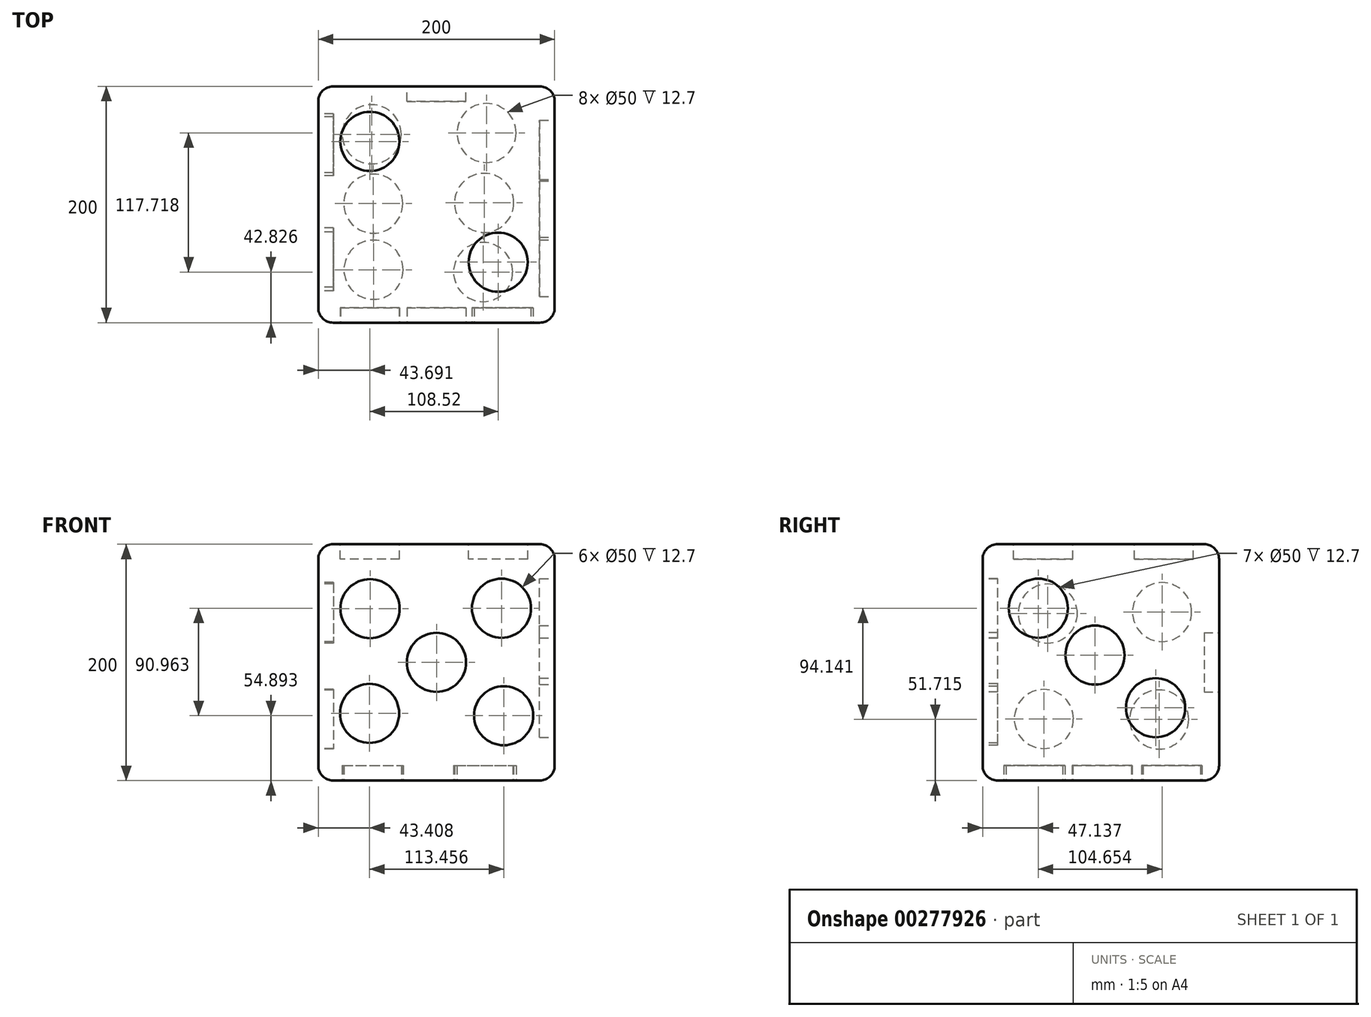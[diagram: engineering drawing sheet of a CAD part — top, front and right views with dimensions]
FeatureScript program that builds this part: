
annotation { "Feature Type Name" : "Feature", "Feature Type Description" : "" }
export const myFeature = defineFeature(function(context is Context, id is Id, definition is map)
    precondition{}
    {
        {
            var Q0;
            Q0=qCreatedBy(makeId("Front.planeOp"),FACE);
            var sketch = newSketch(context, id + "F0", { "sketchPlane" : qUnion([Q0])});
            skLineSegment(sketch, "E0.bottom", {"start": v(100, -100) * mm, "end": v(-100, -100) * mm});
            skLineSegment(sketch, "E0.top", {"start": v(100, 100) * mm, "end": v(-100, 100) * mm});
            skLineSegment(sketch, "E0.left", {"start": v(100, -100) * mm, "end": v(100, 100) * mm});
            skLineSegment(sketch, "E0.right", {"start": v(-100, -100) * mm, "end": v(-100, 100) * mm});
            skPoint(sketch, "E0.middle", {"position": v(0, 0) * mm});
            skSolve(sketch);
        }
        {
            var Q0;
            Q0 = qSketchRegion(id + "F0", true);
            extrude(context, id + "F1", {"entities" : qUnion([Q0]), "depth" : 200 * mm});
        }
        {
            var Q0;
            Q0=makeQuery(id+"F1.opExtrude","SWEPT_FACE",FACE,{"disambiguationData":[OSD([sQuery(id+"F0.wireOp",EDGE,"E0.left")])]});
            var Q1;
            Q1=makeQuery(id+"F1.opExtrude","CAP_FACE",FACE,{"disambiguationData":[OSD([sQuery(id+"F0.wireOp",EDGE,"E0.bottom"),sQuery(id+"F0.wireOp",EDGE,"E0.top"),sQuery(id+"F0.wireOp",EDGE,"E0.left"),sQuery(id+"F0.wireOp",EDGE,"E0.right")])],"isStart":false});
            fillet(context, id + "F2", {"entities" : qUnion([Q0, Q1]), "radius" : 12.7 * mm, "tangentPropagation" : true, "allowEdgeOverflow" : false});
        }
        {
            var Q0;
            Q0=makeQuery(id+"F1.opExtrude","SWEPT_FACE",FACE,{"disambiguationData":[OSD([sQuery(id+"F0.wireOp",EDGE,"E0.right")])]});
            var Q1;
            Q1=makeQuery(id+"F1.opExtrude","SWEPT_FACE",FACE,{"disambiguationData":[OSD([sQuery(id+"F0.wireOp",EDGE,"E0.top")])]});
            var Q2;
            Q2=makeQuery(id+"F1.opExtrude","CAP_FACE",FACE,{"disambiguationData":[OSD([sQuery(id+"F0.wireOp",EDGE,"E0.bottom"),sQuery(id+"F0.wireOp",EDGE,"E0.top"),sQuery(id+"F0.wireOp",EDGE,"E0.left"),sQuery(id+"F0.wireOp",EDGE,"E0.right")])],"isStart":true});
            var Q3;
            Q3=makeQuery(id+"F1.opExtrude","CAP_EDGE",EDGE,{"disambiguationData":[OSD([sQuery(id+"F0.wireOp",EDGE,"E0.right")])],"isStart":true});
            var Q4;
            Q4=makeQuery(id+"F1.opExtrude","SWEPT_FACE",FACE,{"disambiguationData":[OSD([sQuery(id+"F0.wireOp",EDGE,"E0.bottom")])]});
            fillet(context, id + "F3", {"entities" : qUnion([Q0, Q1, Q2, Q3, Q4]), "radius" : 12.7 * mm, "tangentPropagation" : true, "allowEdgeOverflow" : false});
        }
        {
            var Q0;
            Q0=makeQuery(id+"F1.opExtrude","CAP_FACE",FACE,{"disambiguationData":[OSD([sQuery(id+"F0.wireOp",EDGE,"E0.bottom"),sQuery(id+"F0.wireOp",EDGE,"E0.top"),sQuery(id+"F0.wireOp",EDGE,"E0.left"),sQuery(id+"F0.wireOp",EDGE,"E0.right")])],"isStart":true});
            var sketch = newSketch(context, id + "F4", { "sketchPlane" : qUnion([Q0])});
            skCircle(sketch, "E1", {"center": v(0, 0) * mm, "radius": 25 * mm});
            skSolve(sketch);
        }
        {
            var Q0;
            Q0 = qSketchRegion(id + "F4", true);
            extrude(context, id + "F5", {"entities" : qUnion([Q0]), "operationType" : NewBodyOperationType.REMOVE, "oppositeDirection" : true, "depth" : 12.7 * mm});
        }
        {
            var Q0;
            Q0=makeQuery(id+"F1.opExtrude","SWEPT_FACE",FACE,{"disambiguationData":[OSD([sQuery(id+"F0.wireOp",EDGE,"E0.top")])]});
            var sketch = newSketch(context, id + "F6", { "sketchPlane" : qUnion([Q0])});
            skCircle(sketch, "E2", {"center": v(-56.3, -46.63) * mm, "radius": 25 * mm});
            skCircle(sketch, "E3", {"center": v(52.21, -148.81) * mm, "radius": 25 * mm});
            skSolve(sketch);
        }
        {
            var Q0;
            Q0 = qSketchRegion(id + "F6", true);
            extrude(context, id + "F7", {"entities" : qUnion([Q0]), "operationType" : NewBodyOperationType.REMOVE, "oppositeDirection" : true, "depth" : 12.7 * mm});
        }
        {
            var Q0;
            Q0 = qSketchRegion(id + "F6", true);
            extrude(context, id + "F8", {"entities" : qUnion([Q0]), "operationType" : NewBodyOperationType.REMOVE, "oppositeDirection" : true, "depth" : 12.7 * mm});
        }
        {
            var Q0;
            Q0=makeQuery(id+"F1.opExtrude","SWEPT_FACE",FACE,{"disambiguationData":[OSD([sQuery(id+"F0.wireOp",EDGE,"E0.left")])]});
            var sketch = newSketch(context, id + "F9", { "sketchPlane" : qUnion([Q0])});
            skCircle(sketch, "E4", {"center": v(-152.86, 45.86) * mm, "radius": 25 * mm});
            skCircle(sketch, "E5", {"center": v(-104.95, 6.18) * mm, "radius": 25 * mm});
            skCircle(sketch, "E6", {"center": v(-53.66, -38.37) * mm, "radius": 25 * mm});
            skSolve(sketch);
        }
        {
            var Q0;
            Q0 = qSketchRegion(id + "F9", true);
            extrude(context, id + "F10", {"entities" : qUnion([Q0]), "operationType" : NewBodyOperationType.REMOVE, "oppositeDirection" : true, "depth" : 12.7 * mm});
        }
        {
            var Q0;
            Q0=makeQuery(id+"F1.opExtrude","SWEPT_FACE",FACE,{"disambiguationData":[OSD([sQuery(id+"F0.wireOp",EDGE,"E0.right")])]});
            var sketch = newSketch(context, id + "F11", { "sketchPlane" : qUnion([Q0])});
            skCircle(sketch, "E7", {"center": v(50.7, -48.28) * mm, "radius": 25 * mm});
            skCircle(sketch, "E8", {"center": v(48.2, 42.58) * mm, "radius": 25 * mm});
            skCircle(sketch, "E9", {"center": v(144.88, 41.33) * mm, "radius": 25 * mm});
            skCircle(sketch, "E10", {"center": v(148.2, -47.87) * mm, "radius": 25 * mm});
            skSolve(sketch);
        }
        {
            var Q0;
            Q0 = qSketchRegion(id + "F11", true);
            extrude(context, id + "F12", {"entities" : qUnion([Q0]), "operationType" : NewBodyOperationType.REMOVE, "oppositeDirection" : true, "depth" : 12.7 * mm});
        }
        {
            var Q0;
            Q0=makeQuery(id+"F1.opExtrude","CAP_FACE",FACE,{"disambiguationData":[OSD([sQuery(id+"F0.wireOp",EDGE,"E0.bottom"),sQuery(id+"F0.wireOp",EDGE,"E0.top"),sQuery(id+"F0.wireOp",EDGE,"E0.left"),sQuery(id+"F0.wireOp",EDGE,"E0.right")])],"isStart":false});
            var sketch = newSketch(context, id + "F13", { "sketchPlane" : qUnion([Q0])});
            skCircle(sketch, "E11", {"center": v(-56.18, 45.48) * mm, "radius": 25 * mm});
            skCircle(sketch, "E12", {"center": v(-56.6, -43.16) * mm, "radius": 25 * mm});
            skCircle(sketch, "E13", {"center": v(56.86, -45.1) * mm, "radius": 25 * mm});
            skCircle(sketch, "E14", {"center": v(55, 45.86) * mm, "radius": 25 * mm});
            skCircle(sketch, "E15", {"center": v(0, 0) * mm, "radius": 25 * mm});
            skSolve(sketch);
        }
        {
            var Q0;
            Q0 = qSketchRegion(id + "F13", true);
            extrude(context, id + "F14", {"entities" : qUnion([Q0]), "operationType" : NewBodyOperationType.REMOVE, "oppositeDirection" : true, "depth" : 12.7 * mm});
        }
        {
            var Q0;
            Q0=makeQuery(id+"F1.opExtrude","SWEPT_FACE",FACE,{"disambiguationData":[OSD([sQuery(id+"F0.wireOp",EDGE,"E0.bottom")])]});
            var sketch = newSketch(context, id + "F15", { "sketchPlane" : qUnion([Q0])});
            skCircle(sketch, "E16", {"center": v(-53.25, 155.2) * mm, "radius": 25 * mm});
            skCircle(sketch, "E17", {"center": v(-53.45, 99.23) * mm, "radius": 25 * mm});
            skCircle(sketch, "E18", {"center": v(-54.82, 40.6) * mm, "radius": 25 * mm});
            skCircle(sketch, "E19", {"center": v(39.45, 157.17) * mm, "radius": 25 * mm});
            skCircle(sketch, "E20", {"center": v(40.34, 98.6) * mm, "radius": 25 * mm});
            skCircle(sketch, "E21", {"center": v(42.36, 39.46) * mm, "radius": 25 * mm});
            skSolve(sketch);
        }
        {
            var Q0;
            Q0 = qSketchRegion(id + "F15", true);
            extrude(context, id + "F16", {"entities" : qUnion([Q0]), "operationType" : NewBodyOperationType.REMOVE, "oppositeDirection" : true, "depth" : 12.7 * mm});
        }
    });
